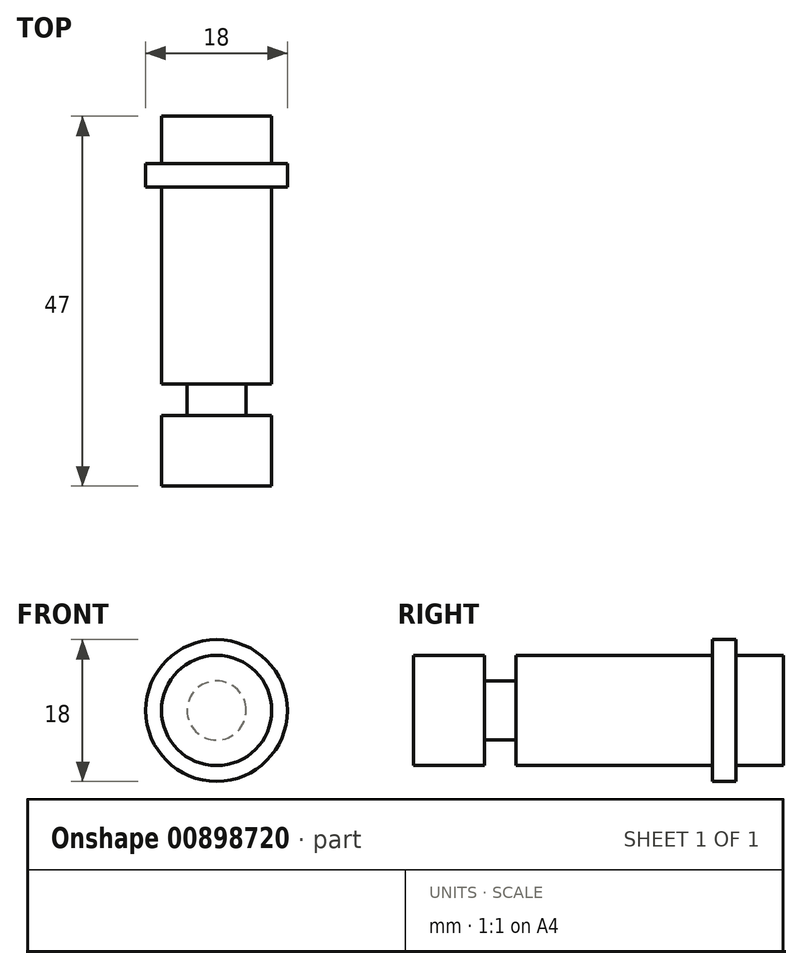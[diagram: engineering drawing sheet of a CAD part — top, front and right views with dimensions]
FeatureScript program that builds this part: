
annotation { "Feature Type Name" : "Feature", "Feature Type Description" : "" }
export const myFeature = defineFeature(function(context is Context, id is Id, definition is map)
    precondition{}
    {
        {
            var Q0;
            Q0=qCreatedBy(makeId("Front.planeOp"),FACE);
            var sketch = newSketch(context, id + "F0", { "sketchPlane" : qUnion([Q0])});
            skCircle(sketch, "E0", {"center": v(0, 0) * mm, "radius": 7 * mm});
            skCircle(sketch, "E1", {"center": v(0, 0) * mm, "radius": 9 * mm});
            skSolve(sketch);
        }
        {
            var Q0;
            Q0=makeQuery(id+"F0.imprint","IMPRINT",FACE,{"disambiguationData":[TD([[makeQuery(id+"F0.imprint","IMPRINT",EDGE,{"derivedFrom":sQuery(id+"F0.wireOp",EDGE,"E0")}),-1.0]])]});
            var Q1;
            Q1=makeQuery(id+"F0.imprint","IMPRINT",FACE,{"disambiguationData":[TD([[makeQuery(id+"F0.imprint","IMPRINT",EDGE,{"derivedFrom":sQuery(id+"F0.wireOp",EDGE,"E0")}),1.0]])]});
            extrude(context, id + "F1", {"entities" : qUnion([Q0, Q1]), "depth" : 3 * mm, "offsetDistance" : 25 * mm});
        }
        {
            var Q0;
            Q0=makeQuery(id+"F0.imprint","IMPRINT",FACE,{"disambiguationData":[TD([[makeQuery(id+"F0.imprint","IMPRINT",EDGE,{"derivedFrom":sQuery(id+"F0.wireOp",EDGE,"E0")}),1.0]])]});
            extrude(context, id + "F2", {"entities" : qUnion([Q0]), "operationType" : NewBodyOperationType.ADD, "oppositeDirection" : true, "depth" : 6 * mm, "offsetDistance" : 25 * mm});
        }
        {
            var Q0;
            Q0=makeQuery(id+"F1.opExtrude","CAP_FACE",FACE,{"disambiguationData":[OSD([sQuery(id+"F0.wireOp",EDGE,"E1")])],"isStart":false});
            var sketch = newSketch(context, id + "F3", { "sketchPlane" : qUnion([Q0])});
            skCircle(sketch, "E2", {"center": v(0, 0) * mm, "radius": 7 * mm});
            skSolve(sketch);
        }
        {
            var Q0;
            Q0 = qSketchRegion(id + "F3", true);
            extrude(context, id + "F4", {"entities" : qUnion([Q0]), "operationType" : NewBodyOperationType.ADD, "depth" : 25 * mm, "offsetDistance" : 25 * mm});
        }
        {
            var Q0;
            Q0=makeQuery(id+"F4.opExtrude","CAP_FACE",FACE,{"disambiguationData":[OSD([sQuery(id+"F3.wireOp",EDGE,"E2")])],"isStart":false});
            var sketch = newSketch(context, id + "F5", { "sketchPlane" : qUnion([Q0])});
            skCircle(sketch, "E3", {"center": v(0, 0) * mm, "radius": 3.75 * mm});
            skSolve(sketch);
        }
        {
            var Q0;
            Q0 = qSketchRegion(id + "F5", true);
            extrude(context, id + "F6", {"entities" : qUnion([Q0]), "operationType" : NewBodyOperationType.ADD, "depth" : 4 * mm, "offsetDistance" : 25 * mm});
        }
        {
            var Q0;
            Q0=makeQuery(id+"F6.opExtrude","CAP_FACE",FACE,{"disambiguationData":[OSD([sQuery(id+"F5.wireOp",EDGE,"E3")])],"isStart":false});
            var sketch = newSketch(context, id + "F7", { "sketchPlane" : qUnion([Q0])});
            skCircle(sketch, "E4", {"center": v(0, 0) * mm, "radius": 7 * mm});
            skSolve(sketch);
        }
        {
            var Q0;
            Q0 = qSketchRegion(id + "F7", true);
            extrude(context, id + "F8", {"entities" : qUnion([Q0]), "operationType" : NewBodyOperationType.ADD, "depth" : 9 * mm, "offsetDistance" : 25 * mm});
        }
    });
